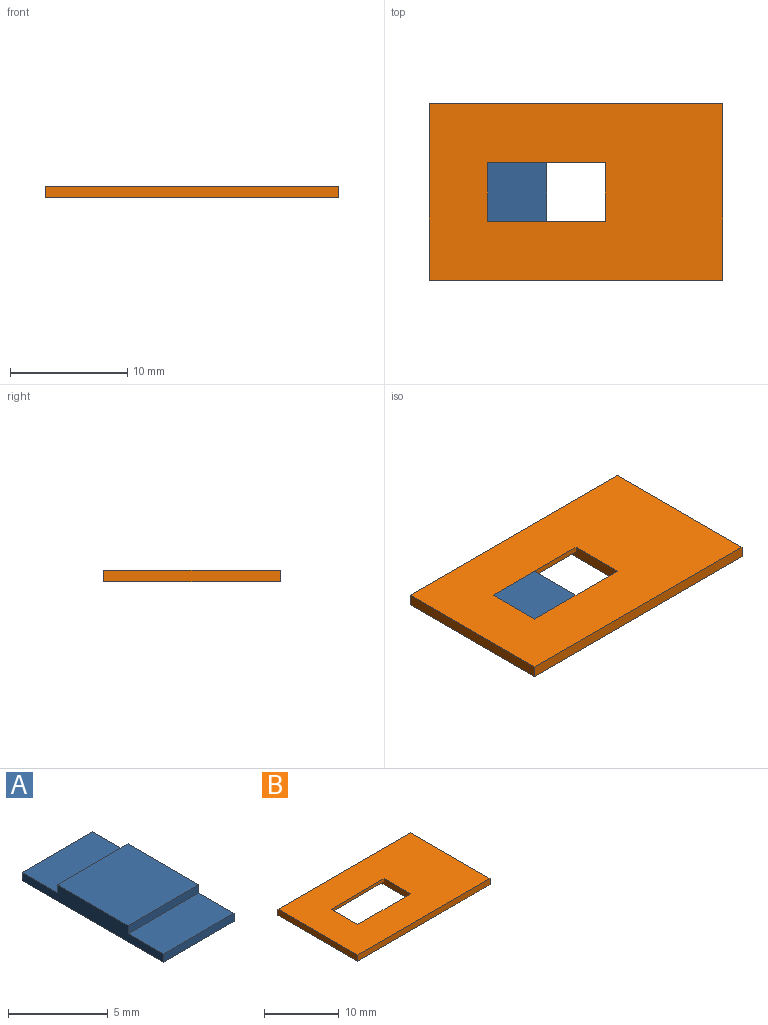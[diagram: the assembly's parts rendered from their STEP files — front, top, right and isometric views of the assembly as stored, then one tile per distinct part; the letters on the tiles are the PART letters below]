
ASSEMBLY  parts=2 mates=1
PART A: 10 faces, bbox 5x10x1 mm
  f0: plane 5x2.5mm, normal (0,0,1), area 12.5mm2, adj f1,f2,f4,f7
  f1: plane 5x0.5mm, normal (0,-1,0), area 2.5mm2, adj f0,f2,f4,f6
  f2: plane 10x1mm, normal (1,0,0), area 7.5mm2, adj f0,f1,f3,f5,f6,f7,f8,f9
  f3: plane 5x0.5mm, normal (0,1,0), area 2.5mm2, adj f2,f4,f5,f6
  f4: plane 10x1mm, normal (-1,0,0), area 7.5mm2, adj f0,f1,f3,f5,f6,f7,f8,f9
  f5: plane 5x2.5mm, normal (0,0,1), area 12.5mm2, adj f2,f3,f4,f8
  f6: plane 10x5mm, normal (0,0,-1), area 50mm2, adj f1,f2,f3,f4
  f7: plane 5x0.5mm, normal (0,-1,0), area 2.5mm2, adj f0,f2,f4,f9
  f8: plane 5x0.5mm, normal (0,1,0), area 2.5mm2, adj f2,f4,f5,f9
  f9: plane 5x5mm, normal (0,0,1), area 25mm2, adj f2,f4,f7,f8
PART B: 14 faces, bbox 25x15x1 mm
  f0: plane 10x0.5mm, normal (0,1,0), area 5mm2, adj f3,f8,f9,f13
  f1: plane 10x0.5mm, normal (0,-1,0), area 5mm2, adj f3,f8,f9,f11
  f2: plane 25x15mm, normal (0,0,-1), area 275mm2, adj f4,f5,f6,f7,f8,f9,f10,f12
  f3: plane 25x15mm, normal (0,0,1), area 325mm2, adj f0,f1,f4,f5,f6,f7,f8,f9
  f4: plane 25x1mm, normal (0,-1,0), area 25mm2, adj f2,f3,f5,f7
  f5: plane 15x1mm, normal (1,0,0), area 15mm2, adj f2,f3,f4,f6
  f6: plane 25x1mm, normal (0,1,0), area 25mm2, adj f2,f3,f5,f7
  f7: plane 15x1mm, normal (-1,0,0), area 15mm2, adj f2,f3,f4,f6
  f8: plane 10x1mm, normal (-1,0,0), area 7.5mm2, adj f0,f1,f2,f3,f10,f11,f12,f13
  f9: plane 10x1mm, normal (1,0,0), area 7.5mm2, adj f0,f1,f2,f3,f10,f11,f12,f13
  f10: plane 10x0.5mm, normal (0,-1,0), area 5mm2, adj f2,f8,f9,f11
  f11: plane 10x2.5mm, normal (0,0,-1), area 25mm2, adj f1,f8,f9,f10
  f12: plane 10x0.5mm, normal (0,1,0), area 5mm2, adj f2,f8,f9,f13
  f13: plane 10x2.5mm, normal (0,0,-1), area 25mm2, adj f0,f8,f9,f12
PLACE A t=(1.81,5.85,6.71)mm
PLACE B t=(6.81,5.85,7.71)mm
MATE planar B.f9 <-> A.f4  axis (1,0,0) through (-0.69,5.85,7.12)mm
